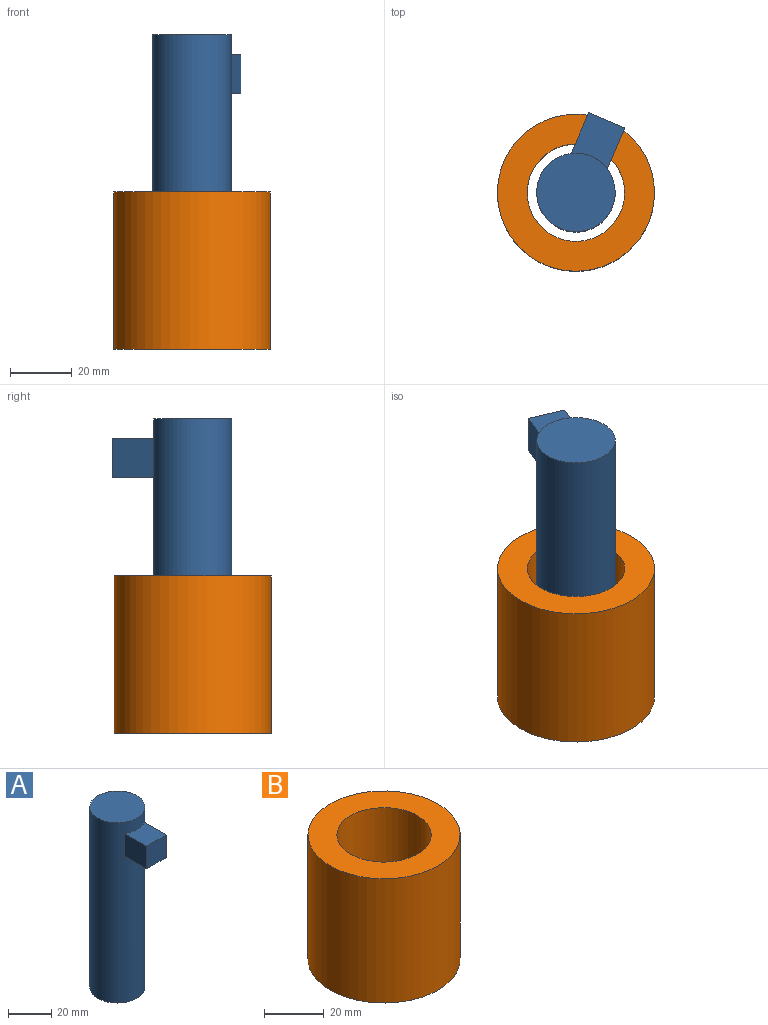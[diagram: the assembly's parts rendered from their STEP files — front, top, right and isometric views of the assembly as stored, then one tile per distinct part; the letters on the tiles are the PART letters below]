
ASSEMBLY  parts=2 mates=2
PART A: 8 faces, bbox 25.4x38.1x101.6 mm
  f0: cylinder r=12.7mm len=101.6mm, axis (0,0,-1), area 7938.4mm2, adj f1,f2,f3,f4,f5,f6
  f1: plane 25.4x25.4mm, normal (0,0,1), area 506.7mm2, adj f0
  f2: plane 25.4x25.4mm, normal (0,0,-1), area 506.7mm2, adj f0
  f3: plane 14.4x12.7mm, normal (-1,0,0), area 182.9mm2, adj f0,f4,f6,f7
  f4: plane 14.4x12.7mm, normal (0,0,-1), area 168.3mm2, adj f0,f3,f5,f7
  f5: plane 14.4x12.7mm, normal (1,0,0), area 182.9mm2, adj f0,f4,f6,f7
  f6: plane 14.4x12.7mm, normal (0,0,1), area 168.3mm2, adj f0,f3,f5,f7
  f7: plane 12.7x12.7mm, normal (0,-1,0), area 161.3mm2, adj f3,f4,f5,f6
PART B: 4 faces, bbox 50.8x50.8x50.8 mm
  f0: cylinder r=15.75mm len=50.8mm, axis (0,0,-1), area 5026.5mm2, adj f2,f3
  f1: cylinder r=25.4mm len=50.8mm, axis (0,0,-1), area 8107.3mm2, adj f2,f3
  f2: plane 50.8x50.8mm, normal (0,0,1), area 1247.7mm2, adj f0,f1
  f3: plane 50.8x50.8mm, normal (0,0,-1), area 1247.7mm2, adj f0,f1
PLACE A rot(axis=(0,0,1),156.9deg) t=(0,0,0)mm
PLACE B rot(axis=(1,0,0),180deg) t=(0,0,50.8)mm
MATE cylindrical A.f0 <-> B.f0  axis (0,0,1) through (0,0,101.6)mm
MATE planar B.f0 <-> A.f0  axis (0,0,-1) through (0,0,0)mm
